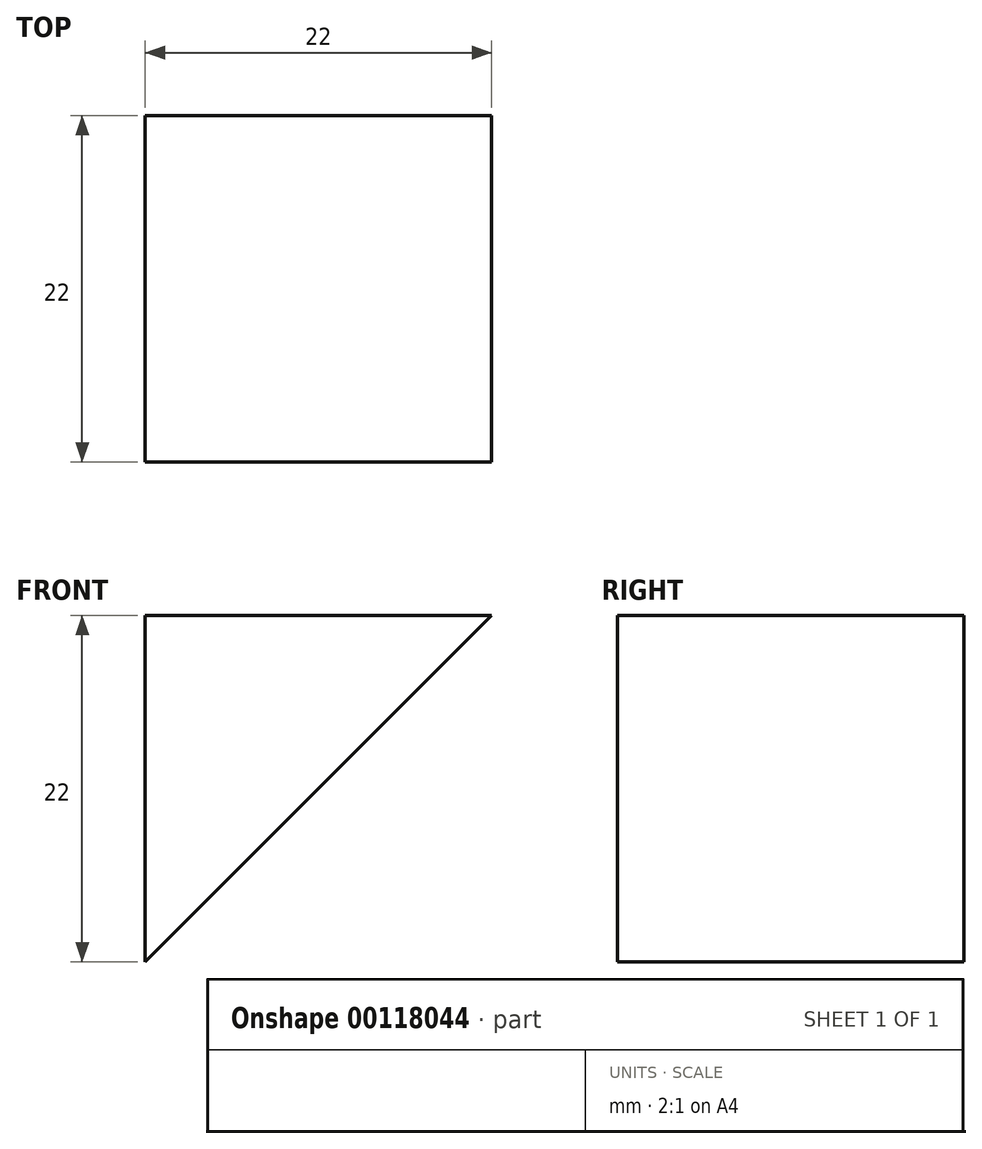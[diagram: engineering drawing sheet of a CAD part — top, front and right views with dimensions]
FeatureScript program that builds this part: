
annotation { "Feature Type Name" : "Feature", "Feature Type Description" : "" }
export const myFeature = defineFeature(function(context is Context, id is Id, definition is map)
    precondition{}
    {
        {
            var Q0;
            Q0=qCreatedBy(makeId("Front.planeOp"),FACE);
            var sketch = newSketch(context, id + "F0", { "sketchPlane" : qUnion([Q0])});
            skLineSegment(sketch, "E0.bottom", {"start": v(2, 0) * mm, "end": v(23, 0) * mm});
            skLineSegment(sketch, "E0.top", {"start": v(2, 25) * mm, "end": v(23, 25) * mm});
            skLineSegment(sketch, "E0.left", {"start": v(0, 2) * mm, "end": v(0, 23) * mm});
            skLineSegment(sketch, "E0.right", {"start": v(25, 2) * mm, "end": v(25, 23) * mm});
            skPoint(sketch, "E1.visualSharp", {"position": v(0, 25) * mm});
            skArc(sketch, "E1.filletArc", {"start": v(2, 25) * mm, "mid": v(0.59, 24.41) * mm, "end": v(0, 23) * mm});
            skPoint(sketch, "E2.visualSharp", {"position": v(25, 25) * mm});
            skArc(sketch, "E2.filletArc", {"start": v(25, 23) * mm, "mid": v(24.41, 24.41) * mm, "end": v(23, 25) * mm});
            skPoint(sketch, "E3.visualSharp", {"position": v(25, 0) * mm});
            skArc(sketch, "E3.filletArc", {"start": v(23, 0) * mm, "mid": v(24.41, 0.59) * mm, "end": v(25, 2) * mm});
            skPoint(sketch, "E4.visualSharp", {"position": v(0, 0) * mm});
            skArc(sketch, "E4.filletArc", {"start": v(0, 2) * mm, "mid": v(0.59, 0.59) * mm, "end": v(2, 0) * mm});
            skLineSegment(sketch, "E5.0", {"start": v(1.5, 23.5) * mm, "end": v(23.5, 23.5) * mm});
            skLineSegment(sketch, "E5.1", {"start": v(1.5, 1.5) * mm, "end": v(1.5, 23.5) * mm});
            skLineSegment(sketch, "E5.2", {"start": v(1.5, 1.5) * mm, "end": v(23.5, 1.5) * mm});
            skLineSegment(sketch, "E5.3", {"start": v(23.5, 1.5) * mm, "end": v(23.5, 23.5) * mm});
            skSolve(sketch);
        }
        {
            var Q0;
            Q0=makeQuery(id+"F0.imprint","IMPRINT",FACE,{"disambiguationData":[TD([[makeQuery(id+"F0.imprint","IMPRINT",EDGE,{"derivedFrom":sQuery(id+"F0.wireOp",EDGE,"E5.0")}),-1.0]])]});
            extrude(context, id + "F1", {"entities" : qUnion([Q0]), "depth" : 22 * mm});
        }
        {
            var Q0;
            Q0=makeQuery(id+"F1.opExtrude","CAP_FACE",FACE,{"disambiguationData":[OSD([sQuery(id+"F0.wireOp",EDGE,"E5.0"),sQuery(id+"F0.wireOp",EDGE,"E5.1"),sQuery(id+"F0.wireOp",EDGE,"E5.2"),sQuery(id+"F0.wireOp",EDGE,"E5.3")])],"isStart":false});
            var sketch = newSketch(context, id + "F2", { "sketchPlane" : qUnion([Q0])});
            skLineSegment(sketch, "E6", {"start": v(1.5, 23.5) * mm, "end": v(23.5, 1.5) * mm});
            skLineSegment(sketch, "E7", {"start": v(1.5, 1.5) * mm, "end": v(23.5, 23.5) * mm});
            skPoint(sketch, "E8", {"position": v(12.5, 12.5) * mm});
            skCircle(sketch, "E9", {"center": v(12.5, 12.5) * mm, "radius": 4 * mm});
            skSolve(sketch);
        }
        {
            var Q0;
            Q0=qCreatedBy(makeId("Top.planeOp"),FACE);
            var Q1;
            Q1=sQuery(id+"F2.wireOp",VERTEX,"E8");
            cPlane(context, id + "F3", {"entities" : qUnion([Q0, Q1]), "cplaneType" : CPlaneType.PLANE_POINT, "offset" : 25 * mm, "width" : 150 * mm, "height" : 150 * mm});
        }
        {
            var Q0;
            Q0=qCreatedBy(id+"F3.planeOp",FACE);
            var sketch = newSketch(context, id + "F4", { "sketchPlane" : qUnion([Q0])});
            skSolve(sketch);
        }
        {
            var Q0;
            {var subQ0=sQuery(id+"F2.wireOp",EDGE,"E7");var subQ1=sQuery(id+"F2.wireOp",EDGE,"E6");var subQ2=makeQuery(id+"F2.imprint","INTERSECT",VERTEX,{"derivedFrom":[subQ1,subQ0]});Q0=makeQuery(id+"F2.imprint","IMPRINT",FACE,{"disambiguationData":[TD([[makeQuery(id+"F2.imprint","IMPRINT",EDGE,{"disambiguationData":[TD([[subQ2,-1.0]])],"derivedFrom":subQ1}),1.0]])]});}
            var Q1;
            {var subQ0=sQuery(id+"F2.wireOp",EDGE,"E9");var subQ1=sQuery(id+"F2.wireOp",EDGE,"E6");var subQ2=makeQuery(id+"F2.imprint","INTERSECT",VERTEX,{"disambiguationData":[OD(0.0)],"derivedFrom":[subQ1,subQ0]});Q1=makeQuery(id+"F2.imprint","IMPRINT",FACE,{"disambiguationData":[TD([[makeQuery(id+"F2.imprint","IMPRINT",EDGE,{"disambiguationData":[TD([[subQ2,-1.0]])],"derivedFrom":subQ1}),1.0]])]});}
            var Q2;
            {var subQ0=sQuery(id+"F2.wireOp",EDGE,"E9");var subQ1=sQuery(id+"F2.wireOp",EDGE,"E6");var subQ2=makeQuery(id+"F2.imprint","INTERSECT",VERTEX,{"disambiguationData":[OD(0.0)],"derivedFrom":[subQ1,subQ0]});Q2=makeQuery(id+"F2.imprint","IMPRINT",FACE,{"disambiguationData":[TD([[makeQuery(id+"F2.imprint","IMPRINT",EDGE,{"disambiguationData":[TD([[subQ2,-1.0]])],"derivedFrom":subQ1}),-1.0]])]});}
            var Q3;
            {var subQ0=sQuery(id+"F2.wireOp",EDGE,"E7");var subQ1=sQuery(id+"F2.wireOp",EDGE,"E6");var subQ2=makeQuery(id+"F2.imprint","INTERSECT",VERTEX,{"derivedFrom":[subQ1,subQ0]});Q3=makeQuery(id+"F2.imprint","IMPRINT",FACE,{"disambiguationData":[TD([[makeQuery(id+"F2.imprint","IMPRINT",EDGE,{"disambiguationData":[TD([[subQ2,-1.0]])],"derivedFrom":subQ1}),-1.0]])]});}
            extrude(context, id + "F5", {"entities" : qUnion([Q0, Q1, Q2, Q3]), "operationType" : NewBodyOperationType.REMOVE, "endBound" : BoundingType.THROUGH_ALL, "oppositeDirection" : true, "depth" : 25 * mm});
        }
    });
